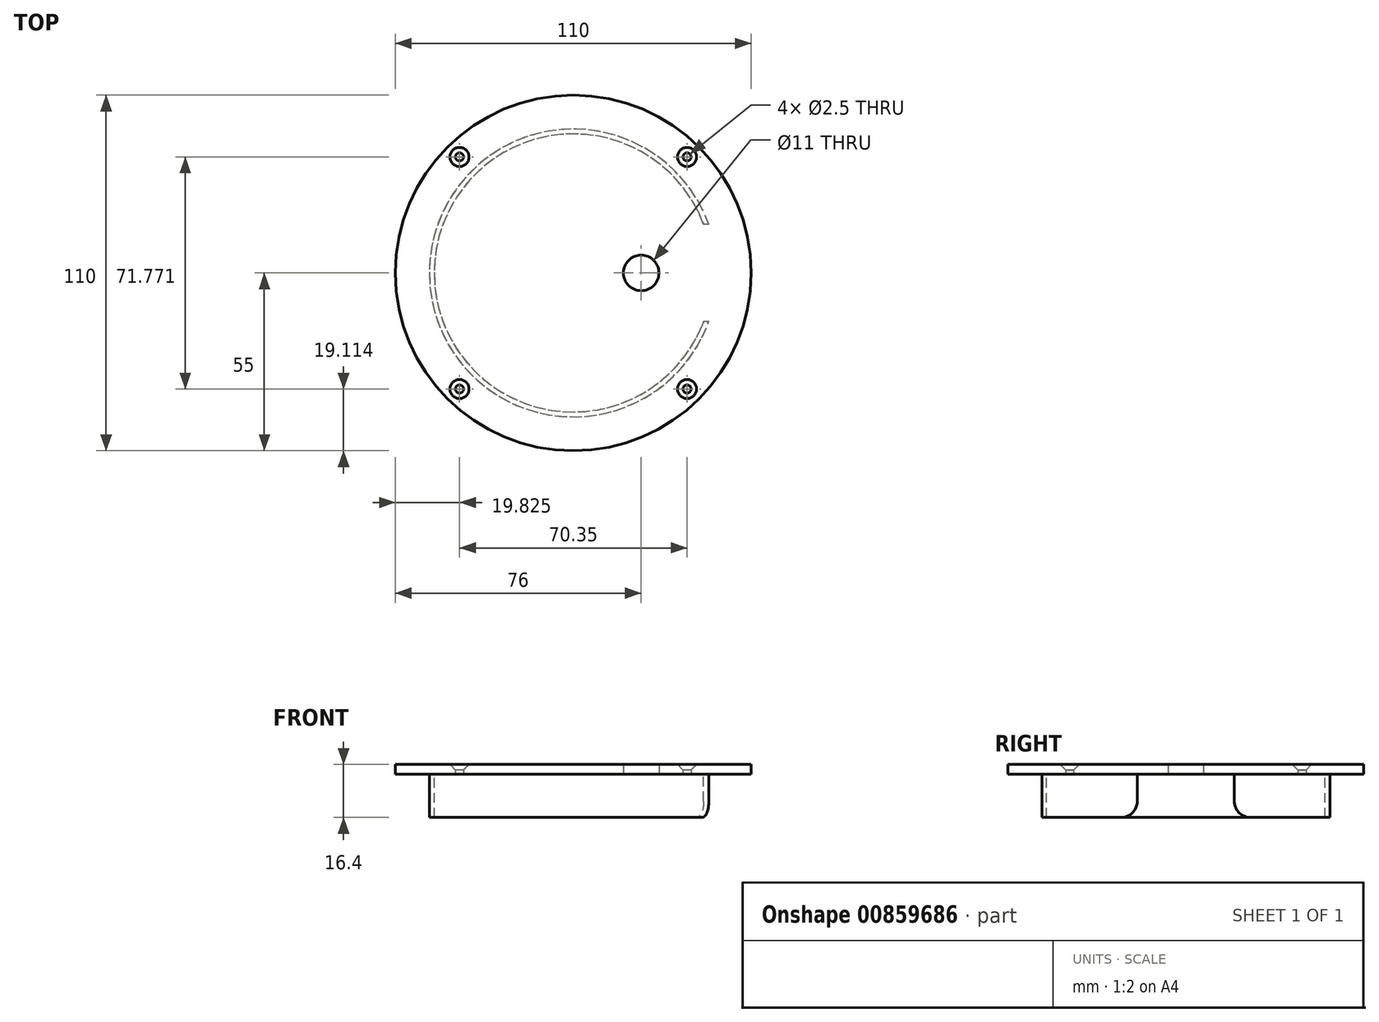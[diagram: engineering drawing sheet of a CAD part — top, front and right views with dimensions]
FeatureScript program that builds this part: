
annotation { "Feature Type Name" : "Feature", "Feature Type Description" : "" }
export const myFeature = defineFeature(function(context is Context, id is Id, definition is map)
    precondition{}
    {
        {
            var Q0;
            Q0=qCreatedBy(makeId("Top.planeOp"),FACE);
            var sketch = newSketch(context, id + "F0", { "sketchPlane" : qUnion([Q0])});
            skArc(sketch, "E0.0.0", {"start": v(45.32, -4.03) * mm, "mid": v(-45.5, 0) * mm, "end": v(45.32, 4.03) * mm});
            skArc(sketch, "E0.0.1", {"start": v(45.32, 4.03) * mm, "mid": v(46.28, 2.09) * mm, "end": v(48.3, 1.3) * mm});
            skLineSegment(sketch, "E0.0.2", {"start": v(48.3, 1.3) * mm, "end": v(54.98, 1.3) * mm});
            skArc(sketch, "E0.0.3", {"start": v(54.98, 1.3) * mm, "mid": v(-55, 0) * mm, "end": v(54.98, -1.3) * mm});
            skLineSegment(sketch, "E0.0.4", {"start": v(54.98, -1.3) * mm, "end": v(48.3, -1.3) * mm});
            skArc(sketch, "E0.0.5", {"start": v(48.3, -1.3) * mm, "mid": v(46.28, -2.09) * mm, "end": v(45.32, -4.03) * mm});
            skLineSegment(sketch, "E1.0.0", {"start": v(32, 1.3) * mm, "end": v(39.27, 1.3) * mm});
            skArc(sketch, "E1.0.1", {"start": v(39.27, 1.3) * mm, "mid": v(41.5, 2.3) * mm, "end": v(42.25, 4.63) * mm});
            skArc(sketch, "E1.0.2", {"start": v(42.25, 4.63) * mm, "mid": v(-42.5, 0) * mm, "end": v(42.25, -4.63) * mm});
            skArc(sketch, "E1.0.3", {"start": v(42.25, -4.63) * mm, "mid": v(41.5, -2.3) * mm, "end": v(39.27, -1.3) * mm});
            skLineSegment(sketch, "E1.0.4", {"start": v(39.27, -1.3) * mm, "end": v(32, -1.3) * mm});
            skLineSegment(sketch, "E1.0.5", {"start": v(32, -1.3) * mm, "end": v(32, -15) * mm});
            skLineSegment(sketch, "E1.0.6", {"start": v(32, -15) * mm, "end": v(21.57, -15) * mm});
            skLineSegment(sketch, "E1.0.7", {"start": v(21.57, -15) * mm, "end": v(21.57, -17.3) * mm});
            skArc(sketch, "E1.0.8", {"start": v(21.57, -17.3) * mm, "mid": v(17.07, -21.8) * mm, "end": v(12.57, -17.3) * mm});
            skLineSegment(sketch, "E1.0.9", {"start": v(12.57, -17.3) * mm, "end": v(12.57, -15) * mm});
            skLineSegment(sketch, "E1.0.10", {"start": v(12.57, -15) * mm, "end": v(-12.57, -15) * mm});
            skLineSegment(sketch, "E1.0.11", {"start": v(-12.57, -15) * mm, "end": v(-12.57, -17.3) * mm});
            skArc(sketch, "E1.0.12", {"start": v(-12.57, -17.3) * mm, "mid": v(-17.07, -21.8) * mm, "end": v(-21.57, -17.3) * mm});
            skLineSegment(sketch, "E1.0.13", {"start": v(-21.57, -17.3) * mm, "end": v(-21.57, -15) * mm});
            skLineSegment(sketch, "E1.0.14", {"start": v(-21.57, -15) * mm, "end": v(-32, -15) * mm});
            skLineSegment(sketch, "E1.0.15", {"start": v(-32, -15) * mm, "end": v(-32, 15) * mm});
            skLineSegment(sketch, "E1.0.16", {"start": v(-32, 15) * mm, "end": v(-21.58, 15) * mm});
            skLineSegment(sketch, "E1.0.17", {"start": v(-21.58, 15) * mm, "end": v(-21.57, 17.3) * mm});
            skArc(sketch, "E1.0.18", {"start": v(-21.57, 17.3) * mm, "mid": v(-17.07, 21.8) * mm, "end": v(-12.57, 17.3) * mm});
            skLineSegment(sketch, "E1.0.19", {"start": v(-12.57, 17.3) * mm, "end": v(-12.57, 15) * mm});
            skLineSegment(sketch, "E1.0.20", {"start": v(-12.57, 15) * mm, "end": v(12.57, 15) * mm});
            skLineSegment(sketch, "E1.0.21", {"start": v(12.57, 15) * mm, "end": v(12.57, 17.3) * mm});
            skArc(sketch, "E1.0.22", {"start": v(12.57, 17.3) * mm, "mid": v(17.07, 21.8) * mm, "end": v(21.57, 17.3) * mm});
            skLineSegment(sketch, "E1.0.23", {"start": v(21.57, 17.3) * mm, "end": v(21.57, 15) * mm});
            skLineSegment(sketch, "E1.0.24", {"start": v(21.57, 15) * mm, "end": v(32, 15) * mm});
            skLineSegment(sketch, "E1.0.25", {"start": v(32, 15) * mm, "end": v(32, 1.3) * mm});
            skCircle(sketch, "E2.0", {"center": v(-35.17, 35.89) * mm, "radius": 1.25 * mm});
            skCircle(sketch, "E3.0", {"center": v(-35.17, -35.89) * mm, "radius": 1.25 * mm});
            skCircle(sketch, "E4.0", {"center": v(35.17, -35.89) * mm, "radius": 1.25 * mm});
            skCircle(sketch, "E5.0", {"center": v(35.17, 35.89) * mm, "radius": 1.25 * mm});
            skLineSegment(sketch, "E6", {"start": v(32, 1.3) * mm, "end": v(32, -1.3) * mm});
            skLineSegment(sketch, "E7", {"start": v(32, 0) * mm, "end": v(21, 0) * mm});
            skCircle(sketch, "E8", {"center": v(21, 0) * mm, "radius": 5.5 * mm});
            skCircle(sketch, "E9", {"center": v(0, 0) * mm, "radius": 55 * mm});
            skSolve(sketch);
        }
        {
            var Q0;
            Q0=makeQuery(id+"F0.imprint","IMPRINT",FACE,{"disambiguationData":[TD([[makeQuery(id+"F0.imprint","IMPRINT",EDGE,{"derivedFrom":sQuery(id+"F0.wireOp",EDGE,"E0.0.0")}),1.0]])]});
            var Q1;
            Q1=makeQuery(id+"F0.imprint","IMPRINT",FACE,{"disambiguationData":[TD([[makeQuery(id+"F0.imprint","IMPRINT",EDGE,{"derivedFrom":sQuery(id+"F0.wireOp",EDGE,"0pVPTYmJ-ZRcT-bwG7-gUaA-FeJE3QAUcCA8")}),1.0]])]});
            var Q2;
            {var subQ0=sQuery(id+"F0.wireOp",EDGE,"E1.0.0");Q2=makeQuery(id+"F0.imprint","IMPRINT",FACE,{"disambiguationData":[TD([[makeQuery(id+"F0.imprint","IMPRINT",EDGE,{"derivedFrom":subQ0}),-1.0]])]});}
            var Q3;
            Q3=makeQuery(id+"F0.imprint","IMPRINT",FACE,{"disambiguationData":[TD([[makeQuery(id+"F0.imprint","IMPRINT",EDGE,{"derivedFrom":sQuery(id+"F0.wireOp",EDGE,"E1.0.0")}),1.0]])]});
            var Q4;
            {var subQ1=sQuery(id+"F0.wireOp",EDGE,"E1.0.5");Q4=makeQuery(id+"F0.imprint","IMPRINT",FACE,{"disambiguationData":[TD([[makeQuery(id+"F0.imprint","IMPRINT",EDGE,{"derivedFrom":subQ1}),-1.0]])]});}
            var Q5;
            Q5=makeQuery(id+"F0.imprint","IMPRINT",FACE,{"disambiguationData":[TD([[makeQuery(id+"F0.imprint","IMPRINT",EDGE,{"derivedFrom":sQuery(id+"F0.wireOp",EDGE,"E0.0.0")}),-1.0]])]});
            extrude(context, id + "F1", {"entities" : qUnion([Q0, Q1, Q2, Q3, Q4, Q5]), "depth" : 3 * mm, "offsetDistance" : 25 * mm});
        }
        {
            var Q0;
            Q0=makeQuery(id+"F1.opExtrude","CAP_FACE",FACE,{"disambiguationData":[OSD([sQuery(id+"F0.wireOp",EDGE,"E2.0"),sQuery(id+"F0.wireOp",EDGE,"E3.0"),sQuery(id+"F0.wireOp",EDGE,"E4.0"),sQuery(id+"F0.wireOp",EDGE,"E5.0"),sQuery(id+"F0.wireOp",EDGE,"E8"),sQuery(id+"F0.wireOp",EDGE,"E9")])],"isStart":true});
            var sketch = newSketch(context, id + "F2", { "sketchPlane" : qUnion([Q0])});
            skCircle(sketch, "E10", {"center": v(0, 0) * mm, "radius": 44.5 * mm});
            skCircle(sketch, "E11", {"center": v(0, 0) * mm, "radius": 43 * mm});
            skLineSegment(sketch, "E12", {"start": v(0, 0) * mm, "end": v(44.5, 0) * mm});
            skLineSegment(sketch, "E13", {"start": v(0, 0) * mm, "end": v(0, 15) * mm});
            skLineSegment(sketch, "E14", {"start": v(0, 15) * mm, "end": v(41.9, 15) * mm});
            skLineSegment(sketch, "E15", {"start": v(41.9, 15) * mm, "end": v(41.9, -15) * mm});
            skLineSegment(sketch, "E16", {"start": v(41.9, -15) * mm, "end": v(0, -15) * mm});
            skLineSegment(sketch, "E17", {"start": v(0, -15) * mm, "end": v(0, 0) * mm});
            skSolve(sketch);
        }
        {
            var Q0;
            {var subQ1=sQuery(id+"F2.wireOp",EDGE,"E14");var subQ6=sQuery(id+"F2.wireOp",EDGE,"E11");var subQ7=makeQuery(id+"F2.imprint","INTERSECT",VERTEX,{"derivedFrom":[subQ6,subQ1]});Q0=makeQuery(id+"F2.imprint","IMPRINT",FACE,{"disambiguationData":[TD([[makeQuery(id+"F2.imprint","IMPRINT",EDGE,{"disambiguationData":[TD([[subQ7,-1.0]])],"derivedFrom":subQ6}),-1.0]])]});}
            extrude(context, id + "F3", {"entities" : qUnion([Q0]), "operationType" : NewBodyOperationType.ADD, "depth" : 13.4 * mm, "offsetDistance" : 25 * mm});
        }
        {
            var Q0;
            Q0=makeQuery(id+"F3.opExtrude","CAP_EDGE",EDGE,{"disambiguationData":[OSD([sQuery(id+"F2.wireOp",EDGE,"E14")])],"isStart":false});
            var Q1;
            Q1=makeQuery(id+"F3.opExtrude","CAP_EDGE",EDGE,{"disambiguationData":[OSD([sQuery(id+"F2.wireOp",EDGE,"E16")])],"isStart":false});
            fillet(context, id + "F4", {"entities" : qUnion([Q0, Q1]), "radius" : 5 * mm, "tangentPropagation" : true, "allowEdgeOverflow" : false});
        }
        {
            var Q0;
            Q0=makeQuery(id+"F1.opExtrude","CAP_EDGE",EDGE,{"disambiguationData":[OSD([sQuery(id+"F0.wireOp",EDGE,"E2.0")])],"isStart":false});
            var Q1;
            Q1=makeQuery(id+"F1.opExtrude","CAP_EDGE",EDGE,{"disambiguationData":[OSD([sQuery(id+"F0.wireOp",EDGE,"E3.0")])],"isStart":false});
            var Q2;
            Q2=makeQuery(id+"F1.opExtrude","CAP_EDGE",EDGE,{"disambiguationData":[OSD([sQuery(id+"F0.wireOp",EDGE,"E4.0")])],"isStart":false});
            var Q3;
            Q3=makeQuery(id+"F1.opExtrude","CAP_EDGE",EDGE,{"disambiguationData":[OSD([sQuery(id+"F0.wireOp",EDGE,"E5.0")])],"isStart":false});
            chamfer(context, id + "F5", {"entities" : qUnion([Q0, Q1, Q2, Q3]), "width" : 1.7 * mm, "tangentPropagation" : true});
        }
    });
